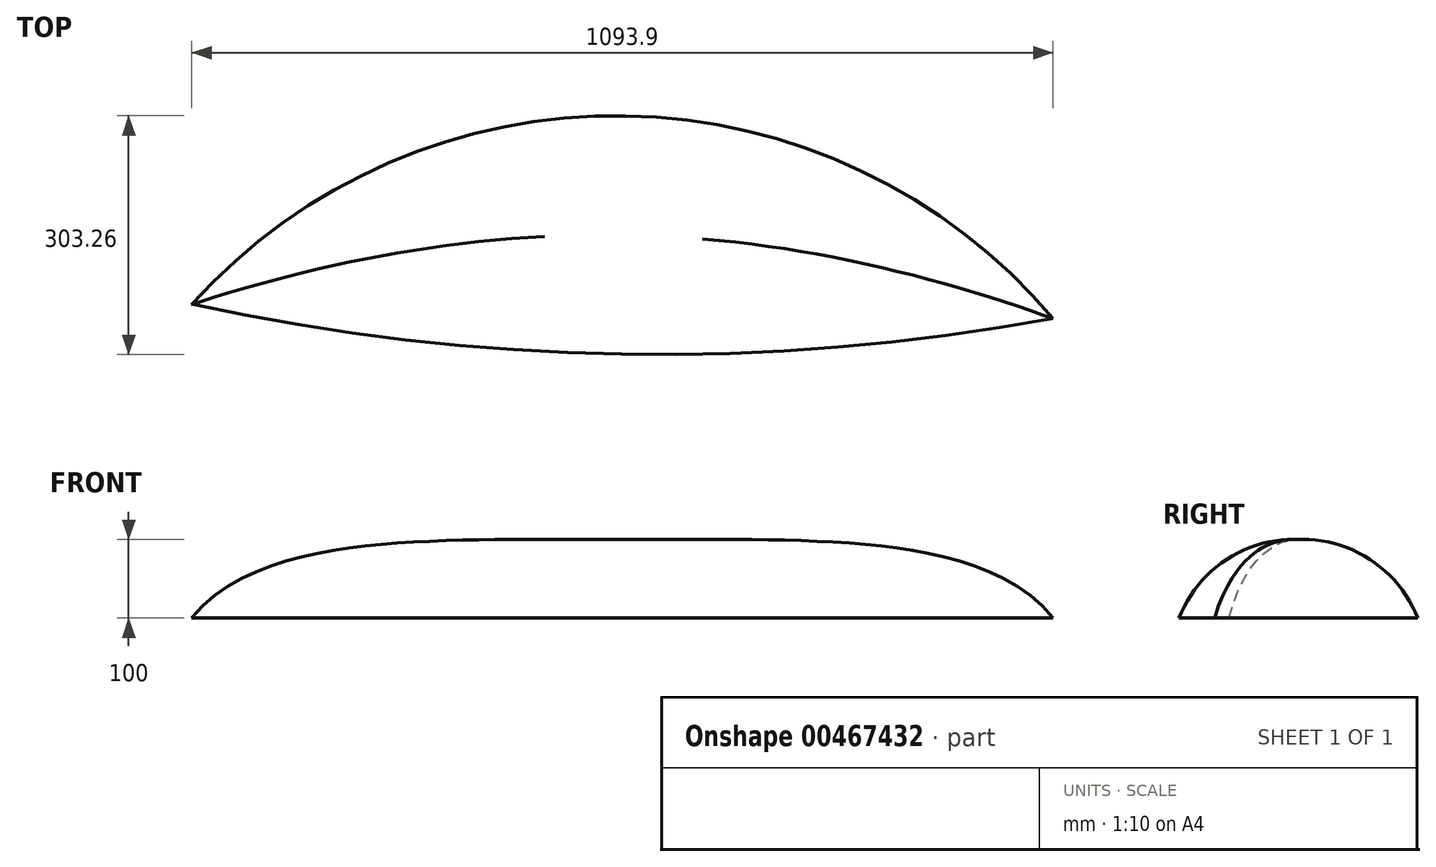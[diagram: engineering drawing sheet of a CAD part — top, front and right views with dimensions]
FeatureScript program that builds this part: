
annotation { "Feature Type Name" : "Feature", "Feature Type Description" : "" }
export const myFeature = defineFeature(function(context is Context, id is Id, definition is map)
    precondition{}
    {
        {
            var Q0;
            Q0=qCreatedBy(makeId("Top.planeOp"),FACE);
            var sketch = newSketch(context, id + "F0", { "sketchPlane" : qUnion([Q0])});
            skArc(sketch, "E0", {"start": v(553.42, -257.58) * mm, "mid": v(10.58, -0.1) * mm, "end": v(-540.48, -239.5) * mm});
            skPoint(sketch, "E0.first.point", {"position": v(-540.48, -239.5) * mm});
            skPoint(sketch, "E0.second.point", {"position": v(0, 0) * mm});
            skPoint(sketch, "E0.third.point", {"position": v(553.42, -257.58) * mm});
            skArc(sketch, "E1", {"start": v(-540.48, -239.5) * mm, "mid": v(5.57, -302.88) * mm, "end": v(553.42, -257.58) * mm});
            skPoint(sketch, "E1.second.point", {"position": v(0, -302.78) * mm});
            skSolve(sketch);
        }
        {
            var Q0;
            Q0=makeQuery(id+"F0.imprint","IMPRINT",FACE,{"disambiguationData":[TD([[makeQuery(id+"F0.imprint","IMPRINT",EDGE,{"derivedFrom":sQuery(id+"F0.wireOp",EDGE,"E0")}),1.0]])]});
            extrude(context, id + "F1", {"entities" : qUnion([Q0]), "depth" : 100 * mm});
        }
        {
            var Q0;
            Q0=makeQuery(id+"F1.opExtrude","CAP_FACE",FACE,{"disambiguationData":[OSD([sQuery(id+"F0.wireOp",EDGE,"E0"),sQuery(id+"F0.wireOp",EDGE,"E1")])],"isStart":false});
            fillet(context, id + "F2", {"entities" : qUnion([Q0]), "radius" : 156.7 * mm, "tangentPropagation" : true, "allowEdgeOverflow" : false});
        }
    });
